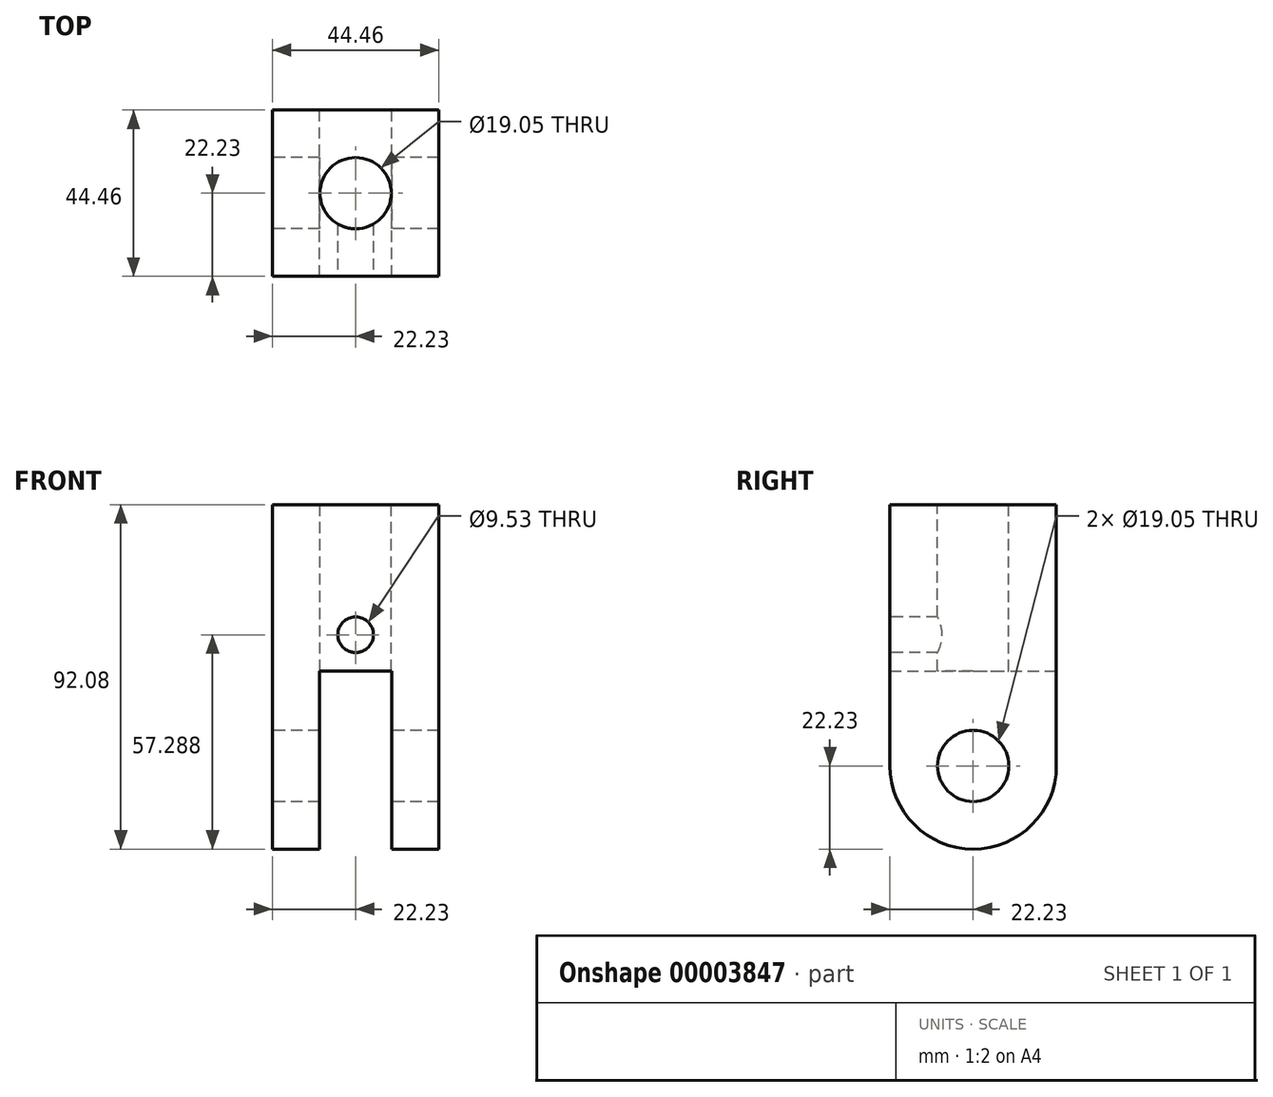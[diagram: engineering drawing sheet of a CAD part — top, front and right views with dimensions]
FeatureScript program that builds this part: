
annotation { "Feature Type Name" : "Feature", "Feature Type Description" : "" }
export const myFeature = defineFeature(function(context is Context, id is Id, definition is map)
    precondition{}
    {
        {
            var Q0;
            Q0=qCreatedBy(makeId("Right.planeOp"),FACE);
            var sketch = newSketch(context, id + "F0", { "sketchPlane" : qUnion([Q0])});
            skCircle(sketch, "E0", {"center": v(0, 0) * mm, "radius": 9.53 * mm});
            skArc(sketch, "E1", {"start": v(-22.23, 0) * mm, "mid": v(0, -22.23) * mm, "end": v(22.23, 0) * mm});
            skLineSegment(sketch, "E2", {"start": v(-22.23, 0) * mm, "end": v(-22.23, 69.85) * mm});
            skLineSegment(sketch, "E3", {"start": v(-22.23, 69.85) * mm, "end": v(0, 69.85) * mm});
            skLineSegment(sketch, "E4.0.MirrorCS", {"start": v(22.23, 0) * mm, "end": v(22.23, 69.85) * mm});
            skLineSegment(sketch, "E5.0.MirrorCS", {"start": v(22.23, 69.85) * mm, "end": v(0, 69.85) * mm});
            skSolve(sketch);
        }
        {
            var Q0;
            Q0 = qSketchRegion(id + "F0", true);
            extrude(context, id + "F1", {"entities" : qUnion([Q0]), "endBound" : BoundingType.SYMMETRIC, "depth" : 44.45 * mm});
        }
        {
            var Q0;
            Q0=makeQuery(id+"F1.opExtrude","SWEPT_FACE",FACE,{"disambiguationData":[OSD([sQuery(id+"F0.wireOp",EDGE,"E4.0.MirrorCS")])]});
            var sketch = newSketch(context, id + "F2", { "sketchPlane" : qUnion([Q0])});
            skLineSegment(sketch, "E6", {"start": v(0, 69.85) * mm, "end": v(0, -28.46) * mm, "construction": true});
            skLineSegment(sketch, "E7.0", {"start": v(-22.23, 25.4) * mm, "end": v(22.23, 25.4) * mm, "construction": true});
            skLineSegment(sketch, "E8.0", {"start": v(-9.65, 69.85) * mm, "end": v(-9.65, -28.46) * mm, "construction": true});
            skLineSegment(sketch, "E9.0.MirrorCS", {"start": v(9.65, 69.85) * mm, "end": v(9.65, -28.46) * mm, "construction": true});
            skLineSegment(sketch, "E10.bottom", {"start": v(-9.65, 25.4) * mm, "end": v(9.65, 25.4) * mm});
            skLineSegment(sketch, "E10.top", {"start": v(-9.65, -28.46) * mm, "end": v(9.65, -28.46) * mm});
            skLineSegment(sketch, "E10.left", {"start": v(-9.65, 25.4) * mm, "end": v(-9.65, -28.46) * mm});
            skLineSegment(sketch, "E10.right", {"start": v(9.65, 25.4) * mm, "end": v(9.65, -28.46) * mm});
            skSolve(sketch);
        }
        {
            var Q0;
            {var subQ6=sQuery(id+"F2.wireOp",EDGE,"E10.top");var subQ7=sQuery(id+"F2.wireOp",EDGE,"E10.bottom");Q0=qUnion([makeQuery(id+"F2.imprint","IMPRINT",FACE,{"disambiguationData":[TD([[makeQuery(id+"F2.imprint","IMPRINT",EDGE,{"derivedFrom":subQ6}),1.0]])]}),makeQuery(id+"F2.imprint","IMPRINT",FACE,{"disambiguationData":[TD([[makeQuery(id+"F2.imprint","IMPRINT",EDGE,{"derivedFrom":subQ7}),-1.0]])]})]);}
            extrude(context, id + "F3", {"entities" : qUnion([Q0]), "operationType" : NewBodyOperationType.REMOVE, "endBound" : BoundingType.THROUGH_ALL, "oppositeDirection" : true, "depth" : 25.4 * mm});
        }
        {
            var Q0;
            Q0=makeQuery(id+"F1.opExtrude","SWEPT_FACE",FACE,{"disambiguationData":[OSD([sQuery(id+"F0.wireOp",EDGE,"E5.0.MirrorCS")])]});
            var sketch = newSketch(context, id + "F4", { "sketchPlane" : qUnion([Q0])});
            skCircle(sketch, "E11", {"center": v(0, 0) * mm, "radius": 9.52 * mm});
            skSolve(sketch);
        }
        {
            var Q0;
            Q0=makeQuery(id+"F4.imprint","IMPRINT",FACE,{"disambiguationData":[TD([[makeQuery(id+"F4.imprint","IMPRINT",EDGE,{"derivedFrom":sQuery(id+"F4.wireOp",EDGE,"E11")}),1.0]])]});
            extrude(context, id + "F5", {"entities" : qUnion([Q0]), "operationType" : NewBodyOperationType.REMOVE, "endBound" : BoundingType.THROUGH_ALL, "oppositeDirection" : true, "depth" : 25.4 * mm});
        }
        {
            var Q0;
            Q0=makeQuery(id+"F1.opExtrude","SWEPT_FACE",FACE,{"disambiguationData":[OSD([sQuery(id+"F0.wireOp",EDGE,"E2")])]});
            var sketch = newSketch(context, id + "F6", { "sketchPlane" : qUnion([Q0])});
            skLineSegment(sketch, "E12.0", {"start": v(22.23, 69.98) * mm, "end": v(-22.23, 69.98) * mm, "construction": true});
            skLineSegment(sketch, "E13.0", {"start": v(22.23, 35.06) * mm, "end": v(-22.23, 35.06) * mm, "construction": true});
            skCircle(sketch, "E14", {"center": v(0, 35.06) * mm, "radius": 4.76 * mm});
            skSolve(sketch);
        }
        {
            var Q0;
            Q0=makeQuery(id+"F6.imprint","IMPRINT",FACE,{"disambiguationData":[TD([[makeQuery(id+"F6.imprint","IMPRINT",EDGE,{"derivedFrom":sQuery(id+"F6.wireOp",EDGE,"E14")}),1.0]])]});
            var Q1;
            Q1=makeQuery(id+"F5.boolean.opBoolean","COPY",FACE,{"derivedFrom":makeQuery(id+"F5.opExtrude","SWEPT_FACE",FACE,{"disambiguationData":[OSD([sQuery(id+"F4.wireOp",EDGE,"E11")])]})});
            extrude(context, id + "F7", {"entities" : qUnion([Q0]), "operationType" : NewBodyOperationType.REMOVE, "endBound" : BoundingType.UP_TO_SURFACE, "oppositeDirection" : true, "endBoundEntityFace" : qUnion([Q1]), "depth" : 25.4 * mm});
        }
    });
